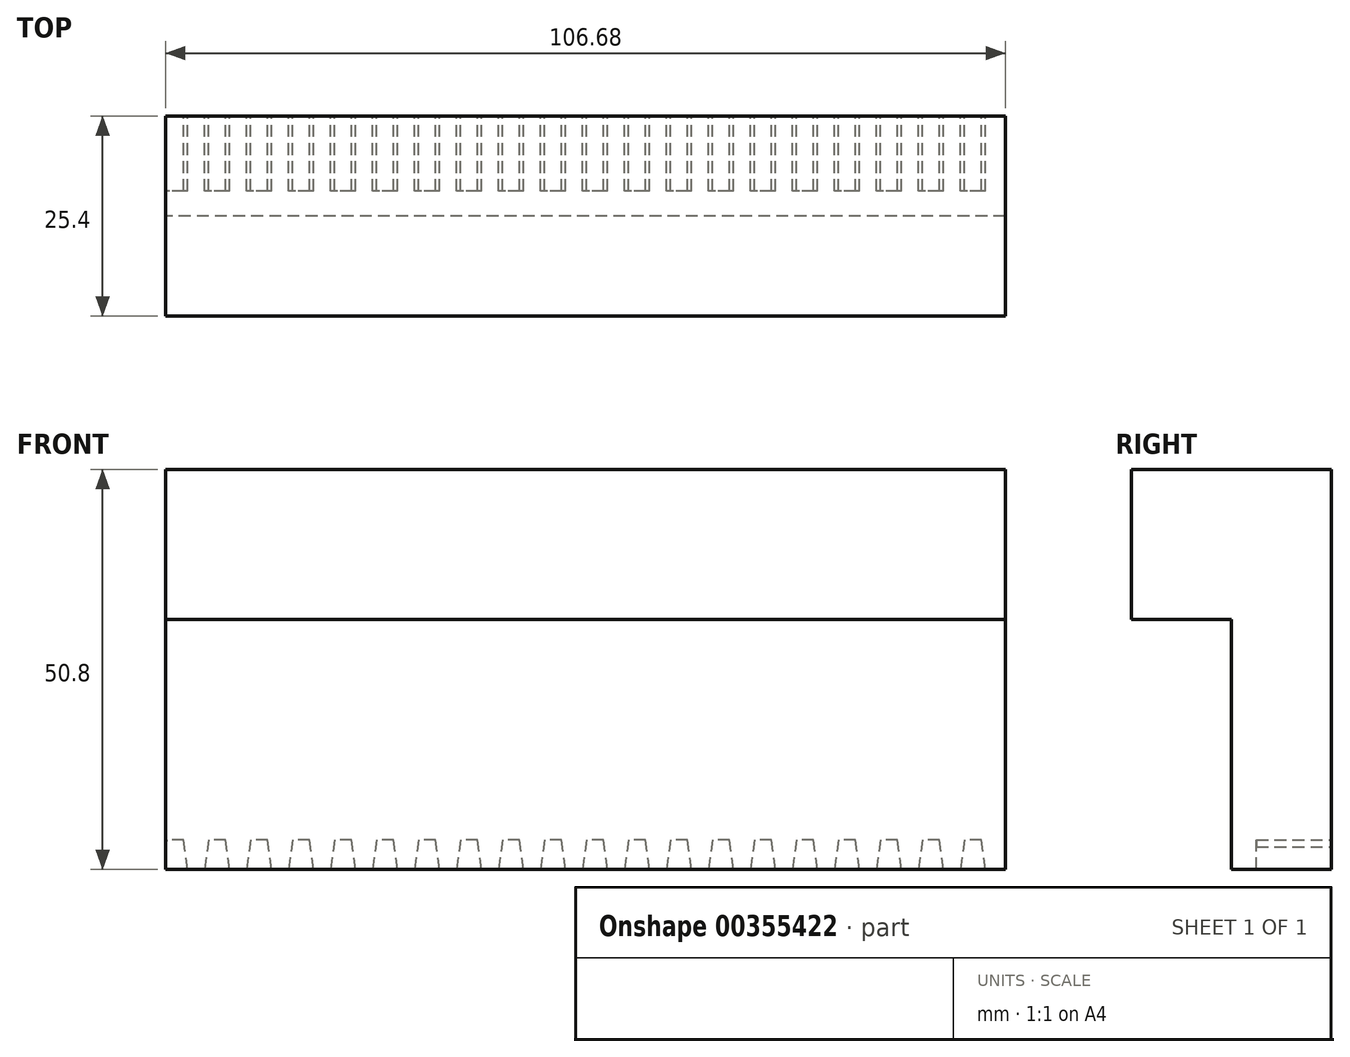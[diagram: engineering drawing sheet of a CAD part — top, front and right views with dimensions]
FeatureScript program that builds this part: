
annotation { "Feature Type Name" : "Feature", "Feature Type Description" : "" }
export const myFeature = defineFeature(function(context is Context, id is Id, definition is map)
    precondition{}
    {
        {
            var Q0;
            Q0=qCreatedBy(makeId("Right.planeOp"),FACE);
            var sketch = newSketch(context, id + "F0", { "sketchPlane" : qUnion([Q0])});
            skLineSegment(sketch, "E0", {"start": v(0, 0) * mm, "end": v(0, 50.8) * mm});
            skLineSegment(sketch, "E1", {"start": v(0, 50.8) * mm, "end": v(-25.4, 50.8) * mm});
            skLineSegment(sketch, "E2", {"start": v(-25.4, 50.8) * mm, "end": v(-25.4, 31.75) * mm});
            skLineSegment(sketch, "E3", {"start": v(-25.4, 31.75) * mm, "end": v(-12.7, 31.75) * mm});
            skLineSegment(sketch, "E4", {"start": v(-12.7, 31.75) * mm, "end": v(-12.7, 0) * mm});
            skLineSegment(sketch, "E5", {"start": v(-12.7, 0) * mm, "end": v(0, 0) * mm});
            skSolve(sketch);
        }
        {
            var Q0;
            Q0=makeQuery(id+"F0.imprint","IMPRINT",FACE,{"disambiguationData":[TD([[makeQuery(id+"F0.imprint","IMPRINT",EDGE,{"derivedFrom":sQuery(id+"F0.wireOp",EDGE,"E0")}),1.0]])]});
            extrude(context, id + "F1", {"entities" : qUnion([Q0]), "depth" : 106.68 * mm});
        }
        {
            var Q0;
            Q0=makeQuery(id+"F1.opExtrude","SWEPT_FACE",FACE,{"disambiguationData":[OSD([sQuery(id+"F0.wireOp",EDGE,"E0")])]});
            var sketch = newSketch(context, id + "F2", { "sketchPlane" : qUnion([Q0])});
            skLineSegment(sketch, "E6", {"start": v(9.52, -2.54) * mm, "end": v(2.54, 0) * mm});
            skLineSegment(sketch, "E7", {"start": v(9.52, -2.54) * mm, "end": v(9.52, 0) * mm});
            skLineSegment(sketch, "E8", {"start": v(2.54, 0) * mm, "end": v(9.52, 0) * mm});
            skLineSegment(sketch, "E9", {"start": v(2.54, 0) * mm, "end": v(2.54, 0) * mm});
            skLineSegment(sketch, "E10", {"start": v(-104.14, 0) * mm, "end": v(-103.64, 3.78) * mm});
            skLineSegment(sketch, "E11", {"start": v(-103.64, 3.78) * mm, "end": v(-101.46, 3.78) * mm});
            skLineSegment(sketch, "E12", {"start": v(-101.46, 3.78) * mm, "end": v(-100.97, 0) * mm});
            skLineSegment(sketch, "E13", {"start": v(-100.97, 0) * mm, "end": v(-104.14, 0) * mm});
            skLineSegment(sketch, "E14.1.0.0", {"start": v(-98.8, 0) * mm, "end": v(-98.3, 3.78) * mm});
            skLineSegment(sketch, "E14.1.0.1", {"start": v(-95.63, 0) * mm, "end": v(-98.8, 0) * mm});
            skLineSegment(sketch, "E14.1.0.2", {"start": v(-98.3, 3.78) * mm, "end": v(-96.13, 3.78) * mm});
            skLineSegment(sketch, "E14.1.0.3", {"start": v(-96.13, 3.78) * mm, "end": v(-95.63, 0) * mm});
            skLineSegment(sketch, "E14.2.0.0", {"start": v(-93.47, 0) * mm, "end": v(-92.97, 3.78) * mm});
            skLineSegment(sketch, "E14.2.0.1", {"start": v(-90.3, 0) * mm, "end": v(-93.47, 0) * mm});
            skLineSegment(sketch, "E14.2.0.2", {"start": v(-92.97, 3.78) * mm, "end": v(-90.8, 3.78) * mm});
            skLineSegment(sketch, "E14.2.0.3", {"start": v(-90.8, 3.78) * mm, "end": v(-90.3, 0) * mm});
            skLineSegment(sketch, "E14.3.0.0", {"start": v(-88.14, 0) * mm, "end": v(-87.64, 3.78) * mm});
            skLineSegment(sketch, "E14.3.0.1", {"start": v(-84.96, 0) * mm, "end": v(-88.14, 0) * mm});
            skLineSegment(sketch, "E14.3.0.2", {"start": v(-87.64, 3.78) * mm, "end": v(-85.46, 3.78) * mm});
            skLineSegment(sketch, "E14.3.0.3", {"start": v(-85.46, 3.78) * mm, "end": v(-84.96, 0) * mm});
            skLineSegment(sketch, "E14.4.0.0", {"start": v(-82.8, 0) * mm, "end": v(-82.3, 3.78) * mm});
            skLineSegment(sketch, "E14.4.0.1", {"start": v(-79.63, 0) * mm, "end": v(-82.8, 0) * mm});
            skLineSegment(sketch, "E14.4.0.2", {"start": v(-82.3, 3.78) * mm, "end": v(-80.13, 3.78) * mm});
            skLineSegment(sketch, "E14.4.0.3", {"start": v(-80.13, 3.78) * mm, "end": v(-79.63, 0) * mm});
            skLineSegment(sketch, "E14.5.0.0", {"start": v(-77.47, 0) * mm, "end": v(-76.97, 3.78) * mm});
            skLineSegment(sketch, "E14.5.0.1", {"start": v(-74.3, 0) * mm, "end": v(-77.47, 0) * mm});
            skLineSegment(sketch, "E14.5.0.2", {"start": v(-76.97, 3.78) * mm, "end": v(-74.8, 3.78) * mm});
            skLineSegment(sketch, "E14.5.0.3", {"start": v(-74.8, 3.78) * mm, "end": v(-74.3, 0) * mm});
            skLineSegment(sketch, "E14.6.0.0", {"start": v(-72.14, 0) * mm, "end": v(-71.64, 3.78) * mm});
            skLineSegment(sketch, "E14.6.0.1", {"start": v(-68.96, 0) * mm, "end": v(-72.14, 0) * mm});
            skLineSegment(sketch, "E14.6.0.2", {"start": v(-71.64, 3.78) * mm, "end": v(-69.46, 3.78) * mm});
            skLineSegment(sketch, "E14.6.0.3", {"start": v(-69.46, 3.78) * mm, "end": v(-68.96, 0) * mm});
            skLineSegment(sketch, "E14.7.0.0", {"start": v(-66.8, 0) * mm, "end": v(-66.3, 3.78) * mm});
            skLineSegment(sketch, "E14.7.0.1", {"start": v(-63.63, 0) * mm, "end": v(-66.8, 0) * mm});
            skLineSegment(sketch, "E14.7.0.2", {"start": v(-66.3, 3.78) * mm, "end": v(-64.12, 3.78) * mm});
            skLineSegment(sketch, "E14.7.0.3", {"start": v(-64.12, 3.78) * mm, "end": v(-63.63, 0) * mm});
            skLineSegment(sketch, "E14.8.0.0", {"start": v(-61.47, 0) * mm, "end": v(-60.97, 3.78) * mm});
            skLineSegment(sketch, "E14.8.0.1", {"start": v(-58.3, 0) * mm, "end": v(-61.47, 0) * mm});
            skLineSegment(sketch, "E14.8.0.2", {"start": v(-60.97, 3.78) * mm, "end": v(-58.8, 3.78) * mm});
            skLineSegment(sketch, "E14.8.0.3", {"start": v(-58.8, 3.78) * mm, "end": v(-58.3, 0) * mm});
            skLineSegment(sketch, "E14.9.0.0", {"start": v(-56.13, 0) * mm, "end": v(-55.64, 3.78) * mm});
            skLineSegment(sketch, "E14.9.0.1", {"start": v(-52.96, 0) * mm, "end": v(-56.13, 0) * mm});
            skLineSegment(sketch, "E14.9.0.2", {"start": v(-55.64, 3.78) * mm, "end": v(-53.46, 3.78) * mm});
            skLineSegment(sketch, "E14.9.0.3", {"start": v(-53.46, 3.78) * mm, "end": v(-52.96, 0) * mm});
            skLineSegment(sketch, "E14.10.0.0", {"start": v(-50.8, 0) * mm, "end": v(-50.3, 3.78) * mm});
            skLineSegment(sketch, "E14.10.0.1", {"start": v(-47.63, 0) * mm, "end": v(-50.8, 0) * mm});
            skLineSegment(sketch, "E14.10.0.2", {"start": v(-50.3, 3.78) * mm, "end": v(-48.12, 3.78) * mm});
            skLineSegment(sketch, "E14.10.0.3", {"start": v(-48.12, 3.78) * mm, "end": v(-47.63, 0) * mm});
            skLineSegment(sketch, "E14.11.0.0", {"start": v(-45.47, 0) * mm, "end": v(-44.97, 3.78) * mm});
            skLineSegment(sketch, "E14.11.0.1", {"start": v(-42.3, 0) * mm, "end": v(-45.47, 0) * mm});
            skLineSegment(sketch, "E14.11.0.2", {"start": v(-44.97, 3.78) * mm, "end": v(-42.79, 3.78) * mm});
            skLineSegment(sketch, "E14.11.0.3", {"start": v(-42.79, 3.78) * mm, "end": v(-42.3, 0) * mm});
            skLineSegment(sketch, "E14.12.0.0", {"start": v(-40.13, 0) * mm, "end": v(-39.63, 3.78) * mm});
            skLineSegment(sketch, "E14.12.0.1", {"start": v(-36.96, 0) * mm, "end": v(-40.13, 0) * mm});
            skLineSegment(sketch, "E14.12.0.2", {"start": v(-39.63, 3.78) * mm, "end": v(-37.45, 3.78) * mm});
            skLineSegment(sketch, "E14.12.0.3", {"start": v(-37.45, 3.78) * mm, "end": v(-36.96, 0) * mm});
            skLineSegment(sketch, "E14.13.0.0", {"start": v(-34.8, 0) * mm, "end": v(-34.3, 3.78) * mm});
            skLineSegment(sketch, "E14.13.0.1", {"start": v(-31.62, 0) * mm, "end": v(-34.8, 0) * mm});
            skLineSegment(sketch, "E14.13.0.2", {"start": v(-34.3, 3.78) * mm, "end": v(-32.12, 3.78) * mm});
            skLineSegment(sketch, "E14.13.0.3", {"start": v(-32.12, 3.78) * mm, "end": v(-31.62, 0) * mm});
            skLineSegment(sketch, "E14.14.0.0", {"start": v(-29.46, 0) * mm, "end": v(-28.97, 3.78) * mm});
            skLineSegment(sketch, "E14.14.0.1", {"start": v(-26.29, 0) * mm, "end": v(-29.46, 0) * mm});
            skLineSegment(sketch, "E14.14.0.2", {"start": v(-28.97, 3.78) * mm, "end": v(-26.79, 3.78) * mm});
            skLineSegment(sketch, "E14.14.0.3", {"start": v(-26.79, 3.78) * mm, "end": v(-26.29, 0) * mm});
            skLineSegment(sketch, "E14.15.0.0", {"start": v(-24.13, 0) * mm, "end": v(-23.63, 3.78) * mm});
            skLineSegment(sketch, "E14.15.0.1", {"start": v(-20.96, 0) * mm, "end": v(-24.13, 0) * mm});
            skLineSegment(sketch, "E14.15.0.2", {"start": v(-23.63, 3.78) * mm, "end": v(-21.45, 3.78) * mm});
            skLineSegment(sketch, "E14.15.0.3", {"start": v(-21.45, 3.78) * mm, "end": v(-20.96, 0) * mm});
            skLineSegment(sketch, "E14.16.0.0", {"start": v(-18.8, 0) * mm, "end": v(-18.3, 3.78) * mm});
            skLineSegment(sketch, "E14.16.0.1", {"start": v(-15.62, 0) * mm, "end": v(-18.8, 0) * mm});
            skLineSegment(sketch, "E14.16.0.2", {"start": v(-18.3, 3.78) * mm, "end": v(-16.12, 3.78) * mm});
            skLineSegment(sketch, "E14.16.0.3", {"start": v(-16.12, 3.78) * mm, "end": v(-15.62, 0) * mm});
            skLineSegment(sketch, "E14.direction1", {"start": v(-104.14, 0) * mm, "end": v(-98.8, 0) * mm, "construction": true});
            skLineSegment(sketch, "E15.0.17.0", {"start": v(-13.46, 0) * mm, "end": v(-12.96, 3.78) * mm});
            skLineSegment(sketch, "E15.3.17.0", {"start": v(-10.29, 0) * mm, "end": v(-13.46, 0) * mm});
            skLineSegment(sketch, "E15.6.17.0", {"start": v(-12.96, 3.78) * mm, "end": v(-10.78, 3.78) * mm});
            skLineSegment(sketch, "E15.9.17.0", {"start": v(-10.78, 3.78) * mm, "end": v(-10.29, 0) * mm});
            skLineSegment(sketch, "E15.0.18.0", {"start": v(-8.13, 0) * mm, "end": v(-7.63, 3.78) * mm});
            skLineSegment(sketch, "E15.3.18.0", {"start": v(-4.95, 0) * mm, "end": v(-8.13, 0) * mm});
            skLineSegment(sketch, "E15.6.18.0", {"start": v(-7.63, 3.78) * mm, "end": v(-5.45, 3.78) * mm});
            skLineSegment(sketch, "E15.9.18.0", {"start": v(-5.45, 3.78) * mm, "end": v(-4.95, 0) * mm});
            skLineSegment(sketch, "E15.0.19.0", {"start": v(-2.8, 0) * mm, "end": v(-2.3, 3.78) * mm});
            skLineSegment(sketch, "E15.3.19.0", {"start": v(0.38, 0) * mm, "end": v(-2.8, 0) * mm});
            skLineSegment(sketch, "E15.6.19.0", {"start": v(-2.3, 3.78) * mm, "end": v(-0.12, 3.78) * mm});
            skLineSegment(sketch, "E15.9.19.0", {"start": v(-0.12, 3.78) * mm, "end": v(0.38, 0) * mm});
            skSolve(sketch);
        }
        {
            var Q0;
            Q0=makeQuery(id+"F2.imprint","IMPRINT",FACE,{"disambiguationData":[TD([[makeQuery(id+"F2.imprint","IMPRINT",EDGE,{"derivedFrom":sQuery(id+"F2.wireOp",EDGE,"E10")}),-1.0]])]});
            var Q1;
            Q1=makeQuery(id+"F2.imprint","IMPRINT",FACE,{"disambiguationData":[TD([[makeQuery(id+"F2.imprint","IMPRINT",EDGE,{"derivedFrom":sQuery(id+"F2.wireOp",EDGE,"E14.1.0.0")}),-1.0]])]});
            var Q2;
            Q2=makeQuery(id+"F2.imprint","IMPRINT",FACE,{"disambiguationData":[TD([[makeQuery(id+"F2.imprint","IMPRINT",EDGE,{"derivedFrom":sQuery(id+"F2.wireOp",EDGE,"E14.2.0.0")}),-1.0]])]});
            var Q3;
            Q3=makeQuery(id+"F2.imprint","IMPRINT",FACE,{"disambiguationData":[TD([[makeQuery(id+"F2.imprint","IMPRINT",EDGE,{"derivedFrom":sQuery(id+"F2.wireOp",EDGE,"E14.3.0.0")}),-1.0]])]});
            var Q4;
            Q4=makeQuery(id+"F2.imprint","IMPRINT",FACE,{"disambiguationData":[TD([[makeQuery(id+"F2.imprint","IMPRINT",EDGE,{"derivedFrom":sQuery(id+"F2.wireOp",EDGE,"E14.4.0.0")}),-1.0]])]});
            var Q5;
            Q5=makeQuery(id+"F2.imprint","IMPRINT",FACE,{"disambiguationData":[TD([[makeQuery(id+"F2.imprint","IMPRINT",EDGE,{"derivedFrom":sQuery(id+"F2.wireOp",EDGE,"E14.5.0.0")}),-1.0]])]});
            var Q6;
            Q6=makeQuery(id+"F2.imprint","IMPRINT",FACE,{"disambiguationData":[TD([[makeQuery(id+"F2.imprint","IMPRINT",EDGE,{"derivedFrom":sQuery(id+"F2.wireOp",EDGE,"E14.6.0.0")}),-1.0]])]});
            var Q7;
            Q7=makeQuery(id+"F2.imprint","IMPRINT",FACE,{"disambiguationData":[TD([[makeQuery(id+"F2.imprint","IMPRINT",EDGE,{"derivedFrom":sQuery(id+"F2.wireOp",EDGE,"E14.7.0.0")}),-1.0]])]});
            var Q8;
            Q8=makeQuery(id+"F2.imprint","IMPRINT",FACE,{"disambiguationData":[TD([[makeQuery(id+"F2.imprint","IMPRINT",EDGE,{"derivedFrom":sQuery(id+"F2.wireOp",EDGE,"E14.8.0.0")}),-1.0]])]});
            var Q9;
            Q9=makeQuery(id+"F2.imprint","IMPRINT",FACE,{"disambiguationData":[TD([[makeQuery(id+"F2.imprint","IMPRINT",EDGE,{"derivedFrom":sQuery(id+"F2.wireOp",EDGE,"E14.9.0.0")}),-1.0]])]});
            var Q10;
            Q10=makeQuery(id+"F2.imprint","IMPRINT",FACE,{"disambiguationData":[TD([[makeQuery(id+"F2.imprint","IMPRINT",EDGE,{"derivedFrom":sQuery(id+"F2.wireOp",EDGE,"E14.10.0.0")}),-1.0]])]});
            var Q11;
            Q11=makeQuery(id+"F2.imprint","IMPRINT",FACE,{"disambiguationData":[TD([[makeQuery(id+"F2.imprint","IMPRINT",EDGE,{"derivedFrom":sQuery(id+"F2.wireOp",EDGE,"E14.11.0.0")}),-1.0]])]});
            var Q12;
            Q12=makeQuery(id+"F2.imprint","IMPRINT",FACE,{"disambiguationData":[TD([[makeQuery(id+"F2.imprint","IMPRINT",EDGE,{"derivedFrom":sQuery(id+"F2.wireOp",EDGE,"E14.12.0.0")}),-1.0]])]});
            var Q13;
            {var subQ0=sQuery(id+"F2.wireOp",EDGE,"E14.16.0.0");Q13=makeQuery(id+"F2.imprint","IMPRINT",FACE,{"disambiguationData":[TD([[makeQuery(id+"F2.imprint","IMPRINT",EDGE,{"derivedFrom":subQ0}),-1.0]])]});}
            var Q14;
            Q14=makeQuery(id+"F2.imprint","IMPRINT",FACE,{"disambiguationData":[TD([[makeQuery(id+"F2.imprint","IMPRINT",EDGE,{"derivedFrom":sQuery(id+"F2.wireOp",EDGE,"E14.15.0.0")}),-1.0]])]});
            var Q15;
            Q15=makeQuery(id+"F2.imprint","IMPRINT",FACE,{"disambiguationData":[TD([[makeQuery(id+"F2.imprint","IMPRINT",EDGE,{"derivedFrom":sQuery(id+"F2.wireOp",EDGE,"E14.14.0.0")}),-1.0]])]});
            var Q16;
            Q16=makeQuery(id+"F2.imprint","IMPRINT",FACE,{"disambiguationData":[TD([[makeQuery(id+"F2.imprint","IMPRINT",EDGE,{"derivedFrom":sQuery(id+"F2.wireOp",EDGE,"E14.13.0.0")}),-1.0]])]});
            var Q17;
            Q17=makeQuery(id+"F2.imprint","IMPRINT",FACE,{"disambiguationData":[TD([[makeQuery(id+"F2.imprint","IMPRINT",EDGE,{"derivedFrom":sQuery(id+"F2.wireOp",EDGE,"E15.0.17.0")}),-1.0]])]});
            var Q18;
            Q18=makeQuery(id+"F2.imprint","IMPRINT",FACE,{"disambiguationData":[TD([[makeQuery(id+"F2.imprint","IMPRINT",EDGE,{"derivedFrom":sQuery(id+"F2.wireOp",EDGE,"E15.0.18.0")}),-1.0]])]});
            var Q19;
            {var subQ7=sQuery(id+"F2.wireOp",EDGE,"E15.0.19.0");Q19=makeQuery(id+"F2.imprint","IMPRINT",FACE,{"disambiguationData":[TD([[makeQuery(id+"F2.imprint","IMPRINT",EDGE,{"derivedFrom":subQ7}),-1.0]])]});}
            extrude(context, id + "F3", {"entities" : qUnion([Q0, Q1, Q2, Q3, Q4, Q5, Q6, Q7, Q8, Q9, Q10, Q11, Q12, Q13, Q14, Q15, Q16, Q17, Q18, Q19]), "operationType" : NewBodyOperationType.REMOVE, "oppositeDirection" : true, "depth" : 9.52 * mm});
        }
    });
